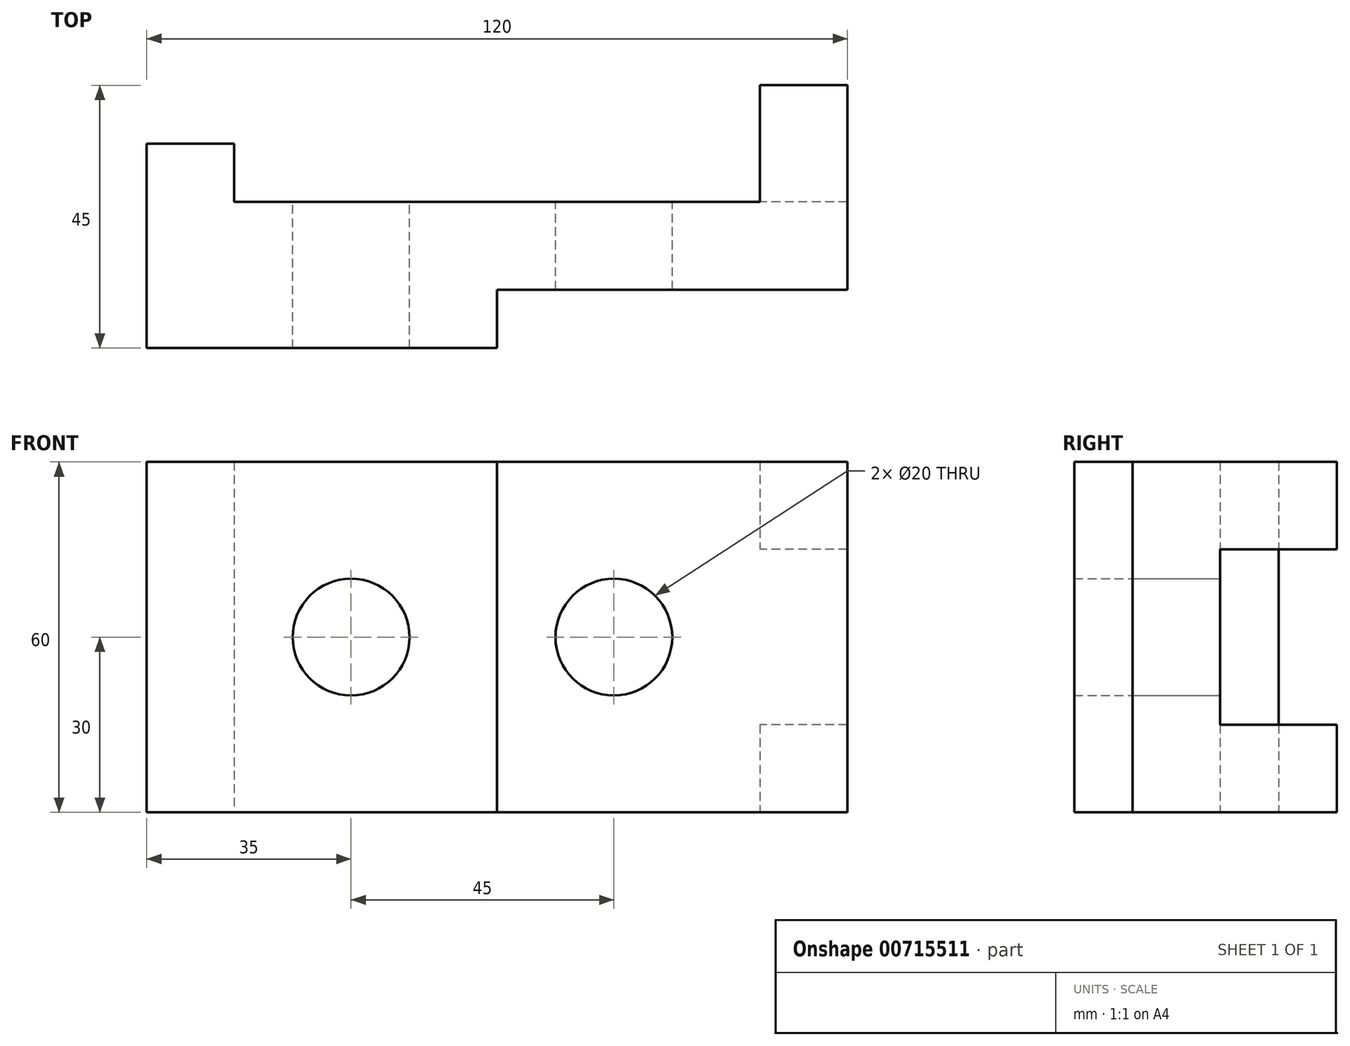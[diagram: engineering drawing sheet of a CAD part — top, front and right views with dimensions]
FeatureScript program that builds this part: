
annotation { "Feature Type Name" : "Feature", "Feature Type Description" : "" }
export const myFeature = defineFeature(function(context is Context, id is Id, definition is map)
    precondition{}
    {
        {
            var Q0;
            Q0=qCreatedBy(makeId("Top.planeOp"),FACE);
            var sketch = newSketch(context, id + "F0", { "sketchPlane" : qUnion([Q0])});
            skLineSegment(sketch, "E0", {"start": v(-73.1, -10.8) * mm, "end": v(-73.1, 24.2) * mm});
            skLineSegment(sketch, "E1", {"start": v(-73.1, 24.2) * mm, "end": v(-58.1, 24.2) * mm});
            skLineSegment(sketch, "E2", {"start": v(-58.1, 24.2) * mm, "end": v(-58.1, 14.2) * mm});
            skLineSegment(sketch, "E3", {"start": v(-58.1, 14.2) * mm, "end": v(31.9, 14.2) * mm});
            skLineSegment(sketch, "E4", {"start": v(31.9, 14.2) * mm, "end": v(31.9, 34.2) * mm});
            skLineSegment(sketch, "E5", {"start": v(31.9, 34.2) * mm, "end": v(46.9, 34.2) * mm});
            skLineSegment(sketch, "E6", {"start": v(46.9, 34.2) * mm, "end": v(46.9, -0.8) * mm});
            skLineSegment(sketch, "E7", {"start": v(46.9, -0.8) * mm, "end": v(-13.1, -0.8) * mm});
            skLineSegment(sketch, "E8", {"start": v(-73.1, -10.8) * mm, "end": v(-13.1, -10.8) * mm});
            skLineSegment(sketch, "E9", {"start": v(-13.1, -10.8) * mm, "end": v(-13.1, -0.8) * mm});
            skSolve(sketch);
        }
        {
            var Q0;
            Q0=makeQuery(id+"F0.imprint","IMPRINT",FACE,{"disambiguationData":[TD([[makeQuery(id+"F0.imprint","IMPRINT",EDGE,{"derivedFrom":sQuery(id+"F0.wireOp",EDGE,"E0")}),-1.0]])]});
            extrude(context, id + "F1", {"entities" : qUnion([Q0]), "depth" : 60 * mm, "offsetDistance" : 25 * mm});
        }
        {
            var Q0;
            Q0=makeQuery(id+"F1.opExtrude","SWEPT_FACE",FACE,{"disambiguationData":[OSD([sQuery(id+"F0.wireOp",EDGE,"E5")])]});
            var sketch = newSketch(context, id + "F2", { "sketchPlane" : qUnion([Q0])});
            skLineSegment(sketch, "E10.bottom", {"start": v(-46.9, 60) * mm, "end": v(-31.9, 60) * mm});
            skLineSegment(sketch, "E10.top", {"start": v(-46.9, 45) * mm, "end": v(-31.9, 45) * mm});
            skLineSegment(sketch, "E10.left", {"start": v(-46.9, 60) * mm, "end": v(-46.9, 45) * mm});
            skLineSegment(sketch, "E10.right", {"start": v(-31.9, 60) * mm, "end": v(-31.9, 45) * mm});
            skLineSegment(sketch, "E11.bottom", {"start": v(-46.9, 0) * mm, "end": v(-31.9, 0) * mm});
            skLineSegment(sketch, "E11.top", {"start": v(-46.9, 15) * mm, "end": v(-31.9, 15) * mm});
            skLineSegment(sketch, "E11.left", {"start": v(-46.9, 0) * mm, "end": v(-46.9, 15) * mm});
            skLineSegment(sketch, "E11.right", {"start": v(-31.9, 0) * mm, "end": v(-31.9, 15) * mm});
            skSolve(sketch);
        }
        {
            var Q0;
            {var subQ0=sQuery(id+"F2.wireOp",EDGE,"E10.top");Q0=makeQuery(id+"F2.imprint","IMPRINT",FACE,{"disambiguationData":[TD([[makeQuery(id+"F2.imprint","IMPRINT",EDGE,{"derivedFrom":subQ0}),-1.0]])]});}
            extrude(context, id + "F3", {"entities" : qUnion([Q0]), "operationType" : NewBodyOperationType.REMOVE, "oppositeDirection" : true, "depth" : 20 * mm, "offsetDistance" : 25 * mm});
        }
        {
            var Q0;
            Q0=makeQuery(id+"F3.boolean.opBoolean","MERGE",FACE,{"derivedFrom":[makeQuery(id+"F1.opExtrude","SWEPT_FACE",FACE,{"disambiguationData":[OSD([sQuery(id+"F0.wireOp",EDGE,"E3")])]}),makeQuery(id+"F3.opExtrude","CAP_FACE",FACE,{"disambiguationData":[OSD([sQuery(id+"F0.wireOp",EDGE,"E4"),sQuery(id+"F0.wireOp",EDGE,"E5"),sQuery(id+"F0.wireOp",EDGE,"E6"),sQuery(id+"F2.wireOp",EDGE,"E10.top"),sQuery(id+"F2.wireOp",EDGE,"E11.top")])],"isStart":false})]});
            var sketch = newSketch(context, id + "F4", { "sketchPlane" : qUnion([Q0])});
            skCircle(sketch, "E12", {"center": v(38.1, 30) * mm, "radius": 10 * mm});
            skCircle(sketch, "E13", {"center": v(-6.9, 30) * mm, "radius": 10 * mm});
            skSolve(sketch);
        }
        {
            var Q0;
            Q0=makeQuery(id+"F4.imprint","IMPRINT",FACE,{"disambiguationData":[TD([[makeQuery(id+"F4.imprint","IMPRINT",EDGE,{"derivedFrom":sQuery(id+"F4.wireOp",EDGE,"E13")}),1.0]])]});
            var Q1;
            Q1=makeQuery(id+"F4.imprint","IMPRINT",FACE,{"disambiguationData":[TD([[makeQuery(id+"F4.imprint","IMPRINT",EDGE,{"derivedFrom":sQuery(id+"F4.wireOp",EDGE,"E12")}),1.0]])]});
            extrude(context, id + "F5", {"entities" : qUnion([Q0, Q1]), "operationType" : NewBodyOperationType.REMOVE, "oppositeDirection" : true, "depth" : 47.6 * mm, "offsetDistance" : 25 * mm});
        }
    });
